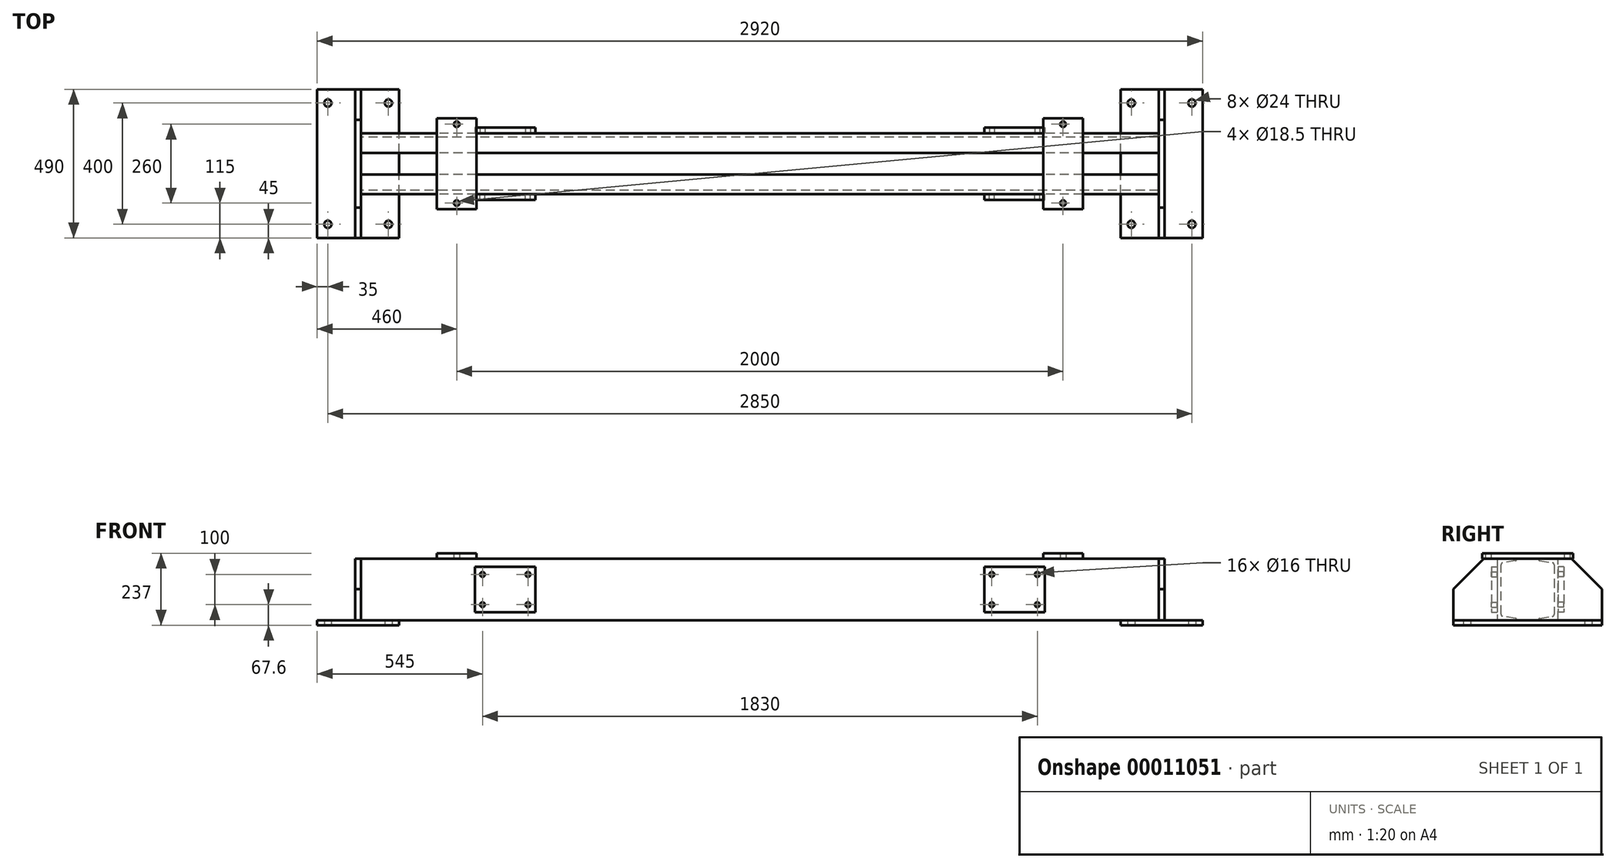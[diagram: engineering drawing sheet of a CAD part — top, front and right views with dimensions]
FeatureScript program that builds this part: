
annotation { "Feature Type Name" : "Feature", "Feature Type Description" : "" }
export const myFeature = defineFeature(function(context is Context, id is Id, definition is map)
    precondition{}
    {
        {
            var Q0;
            Q0=qCreatedBy(makeId("Right.planeOp"),FACE);
            var sketch = newSketch(context, id + "F0", { "sketchPlane" : qUnion([Q0])});
            skLineSegment(sketch, "E0", {"start": v(0, 101.6) * mm, "end": v(0, -114.64) * mm});
            skLineSegment(sketch, "E1", {"start": v(-131.8, 0) * mm, "end": v(140.03, 0) * mm, "construction": true});
            skLineSegment(sketch, "E2.0", {"start": v(-100, 101.6) * mm, "end": v(-100, 0) * mm});
            skLineSegment(sketch, "E3.0", {"start": v(-100, 101.6) * mm, "end": v(-35.8, 101.6) * mm});
            skLineSegment(sketch, "E4.0", {"start": v(-87.6, 81.62) * mm, "end": v(-87.6, 0) * mm});
            skPoint(sketch, "E5.orphan", {"position": v(0, 95.68) * mm});
            skLineSegment(sketch, "E6", {"start": v(-40, 95.12) * mm, "end": v(-81.89, 88.34) * mm});
            skLineSegment(sketch, "E7.0", {"start": v(-35.8, 101.6) * mm, "end": v(-35.8, 100.06) * mm});
            skArc(sketch, "E8.filletArc", {"start": v(-40, 95.12) * mm, "mid": v(-37, 96.82) * mm, "end": v(-35.8, 100.06) * mm});
            skArc(sketch, "E9.filletArc", {"start": v(-81.89, 88.34) * mm, "mid": v(-85.98, 86.03) * mm, "end": v(-87.6, 81.62) * mm});
            skLineSegment(sketch, "E10.trimOffspring", {"start": v(0, 101.6) * mm, "end": v(140.03, 101.6) * mm, "construction": true});
            skLineSegment(sketch, "E11.0.MirrorCS", {"start": v(-35.8, -101.6) * mm, "end": v(-35.8, -100.06) * mm});
            skArc(sketch, "E11.1.MirrorCS", {"start": v(-40, -95.12) * mm, "mid": v(-37, -96.82) * mm, "end": v(-35.8, -100.06) * mm});
            skLineSegment(sketch, "E11.2.MirrorCS", {"start": v(-100, -101.6) * mm, "end": v(-100, 0) * mm});
            skLineSegment(sketch, "E11.3.MirrorCS", {"start": v(-100, -101.6) * mm, "end": v(-35.8, -101.6) * mm});
            skLineSegment(sketch, "E11.4.MirrorCS", {"start": v(-40, -95.12) * mm, "end": v(-81.89, -88.34) * mm});
            skLineSegment(sketch, "E11.5.MirrorCS", {"start": v(-87.6, -81.62) * mm, "end": v(-87.6, 0) * mm});
            skArc(sketch, "E11.6.MirrorCS", {"start": v(-81.89, -88.34) * mm, "mid": v(-85.98, -86.03) * mm, "end": v(-87.6, -81.62) * mm});
            skLineSegment(sketch, "E12.0.MirrorCS", {"start": v(35.8, 101.6) * mm, "end": v(35.8, 100.06) * mm});
            skArc(sketch, "E12.1.MirrorCS", {"start": v(40, 95.12) * mm, "mid": v(37, 96.82) * mm, "end": v(35.8, 100.06) * mm});
            skLineSegment(sketch, "E12.2.MirrorCS", {"start": v(35.8, -101.6) * mm, "end": v(35.8, -100.06) * mm});
            skArc(sketch, "E12.3.MirrorCS", {"start": v(40, -95.12) * mm, "mid": v(37, -96.82) * mm, "end": v(35.8, -100.06) * mm});
            skArc(sketch, "E12.4.MirrorCS", {"start": v(81.89, 88.34) * mm, "mid": v(85.98, 86.03) * mm, "end": v(87.6, 81.62) * mm});
            skLineSegment(sketch, "E12.5.MirrorCS", {"start": v(100, 101.6) * mm, "end": v(100, 0) * mm});
            skLineSegment(sketch, "E12.6.MirrorCS", {"start": v(87.6, 81.62) * mm, "end": v(87.6, 0) * mm});
            skLineSegment(sketch, "E12.7.MirrorCS", {"start": v(100, 101.6) * mm, "end": v(35.8, 101.6) * mm});
            skLineSegment(sketch, "E12.8.MirrorCS", {"start": v(40, 95.12) * mm, "end": v(81.89, 88.34) * mm});
            skLineSegment(sketch, "E12.9.MirrorCS", {"start": v(100, -101.6) * mm, "end": v(35.8, -101.6) * mm});
            skLineSegment(sketch, "E12.10.MirrorCS", {"start": v(87.6, -81.62) * mm, "end": v(87.6, 0) * mm});
            skArc(sketch, "E12.11.MirrorCS", {"start": v(81.89, -88.34) * mm, "mid": v(85.98, -86.03) * mm, "end": v(87.6, -81.62) * mm});
            skLineSegment(sketch, "E12.12.MirrorCS", {"start": v(40, -95.12) * mm, "end": v(81.89, -88.34) * mm});
            skLineSegment(sketch, "E12.13.MirrorCS", {"start": v(100, -101.6) * mm, "end": v(100, 0) * mm});
            skSolve(sketch);
        }
        {
            var Q0;
            Q0 = qSketchRegion(id + "F0", true);
            extrude(context, id + "F1", {"entities" : qUnion([Q0]), "endBound" : BoundingType.SYMMETRIC, "depth" : 2631 * mm});
        }
        {
            var Q0;
            Q0=makeQuery(id+"F1.opExtrude","CAP_FACE",FACE,{"disambiguationData":[OSD([sQuery(id+"F0.wireOp",EDGE,"E12.0.MirrorCS"),sQuery(id+"F0.wireOp",EDGE,"E12.1.MirrorCS"),sQuery(id+"F0.wireOp",EDGE,"E12.2.MirrorCS"),sQuery(id+"F0.wireOp",EDGE,"E12.3.MirrorCS"),sQuery(id+"F0.wireOp",EDGE,"E12.4.MirrorCS"),sQuery(id+"F0.wireOp",EDGE,"E12.5.MirrorCS"),sQuery(id+"F0.wireOp",EDGE,"E12.6.MirrorCS"),sQuery(id+"F0.wireOp",EDGE,"E12.7.MirrorCS"),sQuery(id+"F0.wireOp",EDGE,"E12.8.MirrorCS"),sQuery(id+"F0.wireOp",EDGE,"E12.9.MirrorCS"),sQuery(id+"F0.wireOp",EDGE,"E12.10.MirrorCS"),sQuery(id+"F0.wireOp",EDGE,"E12.11.MirrorCS"),sQuery(id+"F0.wireOp",EDGE,"E12.12.MirrorCS"),sQuery(id+"F0.wireOp",EDGE,"E12.13.MirrorCS")])],"isStart":false});
            var sketch = newSketch(context, id + "F2", { "sketchPlane" : qUnion([Q0])});
            skLineSegment(sketch, "E13", {"start": v(0, 128.92) * mm, "end": v(0, -137.3) * mm, "construction": true});
            skLineSegment(sketch, "E14.0", {"start": v(-245, 101.6) * mm, "end": v(-245, -101.6) * mm});
            skLineSegment(sketch, "E15.0", {"start": v(-245, 101.6) * mm, "end": v(0, 101.6) * mm});
            skLineSegment(sketch, "E16.0", {"start": v(-245, -101.6) * mm, "end": v(0, -101.6) * mm});
            skPoint(sketch, "E17.orphan", {"position": v(-100, 101.6) * mm});
            skPoint(sketch, "E18.orphan", {"position": v(-100, -101.6) * mm});
            skPoint(sketch, "E19.orphan", {"position": v(-35.8, 101.6) * mm});
            skPoint(sketch, "E20.orphan", {"position": v(-35.8, -101.6) * mm});
            skLineSegment(sketch, "E21.0.MirrorCS", {"start": v(245, 101.6) * mm, "end": v(245, -101.6) * mm});
            skLineSegment(sketch, "E22.0.MirrorCS", {"start": v(245, 101.6) * mm, "end": v(0, 101.6) * mm});
            skLineSegment(sketch, "E23.0.MirrorCS", {"start": v(245, -101.6) * mm, "end": v(0, -101.6) * mm});
            skSolve(sketch);
        }
        {
            var Q0;
            Q0 = qSketchRegion(id + "F2", true);
            extrude(context, id + "F3", {"entities" : qUnion([Q0]), "depth" : 19 * mm});
        }
        {
            var Q0;
            Q0=makeQuery(id+"F3.opExtrude","SWEPT_EDGE",EDGE,{"disambiguationData":[OSD([sQuery(id+"F2.wireOp",EDGE,"E14.0"),sQuery(id+"F2.wireOp",EDGE,"E15.0")])]});
            var Q1;
            Q1=makeQuery(id+"F3.opExtrude","SWEPT_EDGE",EDGE,{"disambiguationData":[OSD([sQuery(id+"F2.wireOp",EDGE,"E21.0.MirrorCS"),sQuery(id+"F2.wireOp",EDGE,"E22.0.MirrorCS")])]});
            chamfer(context, id + "F4", {"entities" : qUnion([Q0, Q1]), "width" : 100 * mm, "tangentPropagation" : true});
        }
        {
            var Q0;
            Q0=makeQuery(id+"F1.opExtrude","SWEPT_FACE",FACE,{"disambiguationData":[OSD([sQuery(id+"F0.wireOp",EDGE,"E11.3.MirrorCS")])]});
            var sketch = newSketch(context, id + "F5", { "sketchPlane" : qUnion([Q0])});
            skLineSegment(sketch, "E24.0", {"start": v(1460, -245) * mm, "end": v(1190, -245) * mm});
            skLineSegment(sketch, "E25", {"start": v(1325, 285.85) * mm, "end": v(1325, -304.71) * mm, "construction": true});
            skPoint(sketch, "E26.orphan", {"position": v(1325, -245) * mm});
            skLineSegment(sketch, "E27.0", {"start": v(1460, 245) * mm, "end": v(1460, -245) * mm});
            skLineSegment(sketch, "E28.0.MirrorCS", {"start": v(1190, 245) * mm, "end": v(1190, -245) * mm});
            skPoint(sketch, "E29.orphan", {"position": v(1315.5, -245) * mm});
            skPoint(sketch, "E30.orphan", {"position": v(1334.5, -245) * mm});
            skLineSegment(sketch, "E31.0", {"start": v(1315.5, 245) * mm, "end": v(1315.5, -245) * mm, "construction": true});
            skLineSegment(sketch, "E32", {"start": v(1315.5, 0) * mm, "end": v(1040.75, 0) * mm, "construction": true});
            skPoint(sketch, "E33.orphan", {"position": v(1190, -304.71) * mm});
            skPoint(sketch, "E34.orphan", {"position": v(1460, -304.71) * mm});
            skLineSegment(sketch, "E35.0.MirrorCS", {"start": v(1460, 245) * mm, "end": v(1190, 245) * mm});
            skPoint(sketch, "E36.orphan", {"position": v(1190, 285.85) * mm});
            skPoint(sketch, "E37.orphan", {"position": v(1460, 285.85) * mm});
            skSolve(sketch);
        }
        {
            var Q0;
            Q0 = qSketchRegion(id + "F5", true);
            extrude(context, id + "F6", {"entities" : qUnion([Q0]), "depth" : 16 * mm});
        }
        {
            var Q0;
            Q0=makeQuery(id+"F6.opExtrude","CAP_FACE",FACE,{"disambiguationData":[OSD([sQuery(id+"F5.wireOp",EDGE,"E24.0"),sQuery(id+"F5.wireOp",EDGE,"E27.0"),sQuery(id+"F5.wireOp",EDGE,"E28.0.MirrorCS"),sQuery(id+"F5.wireOp",EDGE,"E35.0.MirrorCS")])],"isStart":false});
            var sketch = newSketch(context, id + "F7", { "sketchPlane" : qUnion([Q0])});
            skLineSegment(sketch, "E38.0.0", {"start": v(1190, 245) * mm, "end": v(1190, -245) * mm, "construction": true});
            skLineSegment(sketch, "E38.0.1", {"start": v(1190, -245) * mm, "end": v(1460, -245) * mm, "construction": true});
            skLineSegment(sketch, "E38.0.2", {"start": v(1460, -245) * mm, "end": v(1460, 245) * mm, "construction": true});
            skLineSegment(sketch, "E38.0.3", {"start": v(1460, 245) * mm, "end": v(1190, 245) * mm, "construction": true});
            skLineSegment(sketch, "E39", {"start": v(1325, 245) * mm, "end": v(1325, -245) * mm, "construction": true});
            skLineSegment(sketch, "E40", {"start": v(1190, 0) * mm, "end": v(1460, 0) * mm, "construction": true});
            skLineSegment(sketch, "E41.0", {"start": v(1225, 245) * mm, "end": v(1225, -245) * mm, "construction": true});
            skLineSegment(sketch, "E42.0", {"start": v(1190, -200) * mm, "end": v(1460, -200) * mm, "construction": true});
            skCircle(sketch, "E43", {"center": v(1225, -200) * mm, "radius": 12 * mm});
            skCircle(sketch, "E44.0.MirrorC", {"center": v(1225, 200) * mm, "radius": 12 * mm});
            skCircle(sketch, "E45.0.MirrorC", {"center": v(1425, 200) * mm, "radius": 12 * mm});
            skCircle(sketch, "E46.0.MirrorC", {"center": v(1425, -200) * mm, "radius": 12 * mm});
            skSolve(sketch);
        }
        {
            var Q0;
            Q0 = qSketchRegion(id + "F7", true);
            extrude(context, id + "F8", {"entities" : qUnion([Q0]), "operationType" : NewBodyOperationType.REMOVE, "endBound" : BoundingType.THROUGH_ALL, "oppositeDirection" : true, "depth" : 25 * mm});
        }
        {
            var Q0;
            Q0=makeQuery(id+"F1.opExtrude","SWEPT_FACE",FACE,{"disambiguationData":[OSD([sQuery(id+"F0.wireOp",EDGE,"E3.0")])]});
            var sketch = newSketch(context, id + "F9", { "sketchPlane" : qUnion([Q0])});
            skLineSegment(sketch, "E47", {"start": v(0, 252.03) * mm, "end": v(0, -313.66) * mm, "construction": true});
            skLineSegment(sketch, "E48", {"start": v(-286.53, 0) * mm, "end": v(1117.78, 0) * mm, "construction": true});
            skLineSegment(sketch, "E49.0", {"start": v(1000, 252.03) * mm, "end": v(1000, -313.66) * mm, "construction": true});
            skLineSegment(sketch, "E50.0", {"start": v(1065, 150) * mm, "end": v(1065, -150) * mm});
            skLineSegment(sketch, "E51.0", {"start": v(935, 150) * mm, "end": v(1065, 150) * mm});
            skLineSegment(sketch, "E52.0.MirrorCS", {"start": v(935, -150) * mm, "end": v(1065, -150) * mm});
            skLineSegment(sketch, "E53.0.MirrorCS", {"start": v(935, 150) * mm, "end": v(935, -150) * mm});
            skPoint(sketch, "E54.orphan", {"position": v(-286.53, 150) * mm});
            skPoint(sketch, "E55.orphan", {"position": v(-286.53, -150) * mm});
            skPoint(sketch, "E56.orphan", {"position": v(935, 252.03) * mm});
            skPoint(sketch, "E57.orphan", {"position": v(1065, 252.03) * mm});
            skPoint(sketch, "E58.orphan", {"position": v(1117.78, 150) * mm});
            skPoint(sketch, "E59.orphan", {"position": v(1117.78, -150) * mm});
            skPoint(sketch, "E60.orphan", {"position": v(1065, -313.66) * mm});
            skPoint(sketch, "E61.orphan", {"position": v(935, -313.66) * mm});
            skLineSegment(sketch, "E62.0", {"start": v(-286.53, 130) * mm, "end": v(1117.78, 130) * mm, "construction": true});
            skCircle(sketch, "E63", {"center": v(1000, 130) * mm, "radius": 9.25 * mm});
            skCircle(sketch, "E64.0.MirrorC", {"center": v(1000, -130) * mm, "radius": 9.25 * mm});
            skSolve(sketch);
        }
        {
            var Q0;
            Q0 = qSketchRegion(id + "F9", true);
            extrude(context, id + "F10", {"entities" : qUnion([Q0]), "depth" : 17.8 * mm});
        }
        {
            var Q0;
            Q0=makeQuery(id+"F1.opExtrude","SWEPT_FACE",FACE,{"disambiguationData":[OSD([sQuery(id+"F0.wireOp",EDGE,"E2.0"),sQuery(id+"F0.wireOp",EDGE,"E11.2.MirrorCS")])]});
            var sketch = newSketch(context, id + "F11", { "sketchPlane" : qUnion([Q0])});
            skLineSegment(sketch, "E65", {"start": v(0, 304.08) * mm, "end": v(0, -303.44) * mm, "construction": true});
            skLineSegment(sketch, "E66.0", {"start": v(840, 304.08) * mm, "end": v(840, -303.44) * mm, "construction": true});
            skLineSegment(sketch, "E67.0", {"start": v(940, 75) * mm, "end": v(940, -75) * mm});
            skLineSegment(sketch, "E68", {"start": v(0, 0) * mm, "end": v(1430.05, 0) * mm, "construction": true});
            skLineSegment(sketch, "E69.0", {"start": v(740, 75) * mm, "end": v(940, 75) * mm});
            skLineSegment(sketch, "E70.0.MirrorCS", {"start": v(740, -75) * mm, "end": v(940, -75) * mm});
            skLineSegment(sketch, "E71.0.MirrorCS", {"start": v(740, 75) * mm, "end": v(740, -75) * mm});
            skPoint(sketch, "E72.orphan", {"position": v(0, 75) * mm});
            skPoint(sketch, "E73.orphan", {"position": v(0, -75) * mm});
            skPoint(sketch, "E74.orphan", {"position": v(1430.05, -75) * mm});
            skPoint(sketch, "E75.orphan", {"position": v(1430.05, 75) * mm});
            skPoint(sketch, "E76.orphan", {"position": v(940, 304.08) * mm});
            skPoint(sketch, "E77.orphan", {"position": v(740, 304.08) * mm});
            skPoint(sketch, "E78.orphan", {"position": v(740, -303.44) * mm});
            skPoint(sketch, "E79.orphan", {"position": v(940, -303.44) * mm});
            skLineSegment(sketch, "E80.0", {"start": v(765, 304.08) * mm, "end": v(765, -303.44) * mm, "construction": true});
            skLineSegment(sketch, "E81.0", {"start": v(0, -50) * mm, "end": v(1430.05, -50) * mm, "construction": true});
            skCircle(sketch, "E82", {"center": v(765, -50) * mm, "radius": 8 * mm});
            skCircle(sketch, "E83.0.MirrorC", {"center": v(765, 50) * mm, "radius": 8 * mm});
            skCircle(sketch, "E84.0.MirrorC", {"center": v(915, -50) * mm, "radius": 8 * mm});
            skCircle(sketch, "E85.0.MirrorC", {"center": v(915, 50) * mm, "radius": 8 * mm});
            skSolve(sketch);
        }
        {
            var Q0;
            Q0 = qSketchRegion(id + "F11", true);
            extrude(context, id + "F12", {"entities" : qUnion([Q0]), "depth" : 19 * mm});
        }
        {
            var Q0;
            Q0=makeQuery(id+"F12.opExtrude","SWEPT_BODY",BODY,{"disambiguationData":[OSD([sQuery(id+"F11.wireOp",EDGE,"E67.0"),sQuery(id+"F11.wireOp",EDGE,"E69.0"),sQuery(id+"F11.wireOp",EDGE,"E70.0.MirrorCS"),sQuery(id+"F11.wireOp",EDGE,"E71.0.MirrorCS"),sQuery(id+"F11.wireOp",EDGE,"E82"),sQuery(id+"F11.wireOp",EDGE,"E83.0.MirrorC"),sQuery(id+"F11.wireOp",EDGE,"E84.0.MirrorC"),sQuery(id+"F11.wireOp",EDGE,"E85.0.MirrorC")])]});
            var Q1;
            Q1=qCreatedBy(makeId("Front.planeOp"),FACE);
            mirror(context, id + "F13", {"entities" : qUnion([Q0]), "mirrorPlane" : qUnion([Q1])});
        }
        {
            var Q0;
            Q0=makeQuery(id+"F3.opExtrude","SWEPT_BODY",BODY,{"disambiguationData":[OSD([sQuery(id+"F2.wireOp",EDGE,"E14.0"),sQuery(id+"F2.wireOp",EDGE,"E15.0"),sQuery(id+"F2.wireOp",EDGE,"E16.0"),sQuery(id+"F2.wireOp",EDGE,"E21.0.MirrorCS"),sQuery(id+"F2.wireOp",EDGE,"E22.0.MirrorCS"),sQuery(id+"F2.wireOp",EDGE,"E23.0.MirrorCS")])]});
            var Q1;
            Q1=makeQuery(id+"F6.opExtrude","SWEPT_BODY",BODY,{"disambiguationData":[OSD([sQuery(id+"F5.wireOp",EDGE,"E24.0"),sQuery(id+"F5.wireOp",EDGE,"E27.0"),sQuery(id+"F5.wireOp",EDGE,"E28.0.MirrorCS"),sQuery(id+"F5.wireOp",EDGE,"E35.0.MirrorCS")])]});
            var Q2;
            Q2=makeQuery(id+"F10.opExtrude","SWEPT_BODY",BODY,{"disambiguationData":[OSD([sQuery(id+"F9.wireOp",EDGE,"E50.0"),sQuery(id+"F9.wireOp",EDGE,"E51.0"),sQuery(id+"F9.wireOp",EDGE,"E52.0.MirrorCS"),sQuery(id+"F9.wireOp",EDGE,"E53.0.MirrorCS"),sQuery(id+"F9.wireOp",EDGE,"E63"),sQuery(id+"F9.wireOp",EDGE,"E64.0.MirrorC")])]});
            var Q3;
            Q3=makeQuery(id+"F12.opExtrude","SWEPT_BODY",BODY,{"disambiguationData":[OSD([sQuery(id+"F11.wireOp",EDGE,"E67.0"),sQuery(id+"F11.wireOp",EDGE,"E69.0"),sQuery(id+"F11.wireOp",EDGE,"E70.0.MirrorCS"),sQuery(id+"F11.wireOp",EDGE,"E71.0.MirrorCS"),sQuery(id+"F11.wireOp",EDGE,"E82"),sQuery(id+"F11.wireOp",EDGE,"E83.0.MirrorC"),sQuery(id+"F11.wireOp",EDGE,"E84.0.MirrorC"),sQuery(id+"F11.wireOp",EDGE,"E85.0.MirrorC")])]});
            var Q4;
            Q4=qCreatedBy(makeId("Right.planeOp"),FACE);
            mirror(context, id + "F14", {"entities" : qUnion([Q0, Q1, Q2, Q3]), "mirrorPlane" : qUnion([Q4])});
        }
        {
            var Q0;
            Q0=makeQuery(id+"F13.opPattern","COPY",BODY,{"derivedFrom":makeQuery(id+"F12.opExtrude","SWEPT_BODY",BODY,{"disambiguationData":[OSD([sQuery(id+"F11.wireOp",EDGE,"E67.0"),sQuery(id+"F11.wireOp",EDGE,"E69.0"),sQuery(id+"F11.wireOp",EDGE,"E70.0.MirrorCS"),sQuery(id+"F11.wireOp",EDGE,"E71.0.MirrorCS"),sQuery(id+"F11.wireOp",EDGE,"E82"),sQuery(id+"F11.wireOp",EDGE,"E83.0.MirrorC"),sQuery(id+"F11.wireOp",EDGE,"E84.0.MirrorC"),sQuery(id+"F11.wireOp",EDGE,"E85.0.MirrorC")])]}),"instanceName":"1"});
            var Q1;
            Q1=qCreatedBy(makeId("Right.planeOp"),FACE);
            mirror(context, id + "F15", {"entities" : qUnion([Q0]), "mirrorPlane" : qUnion([Q1])});
        }
    });
